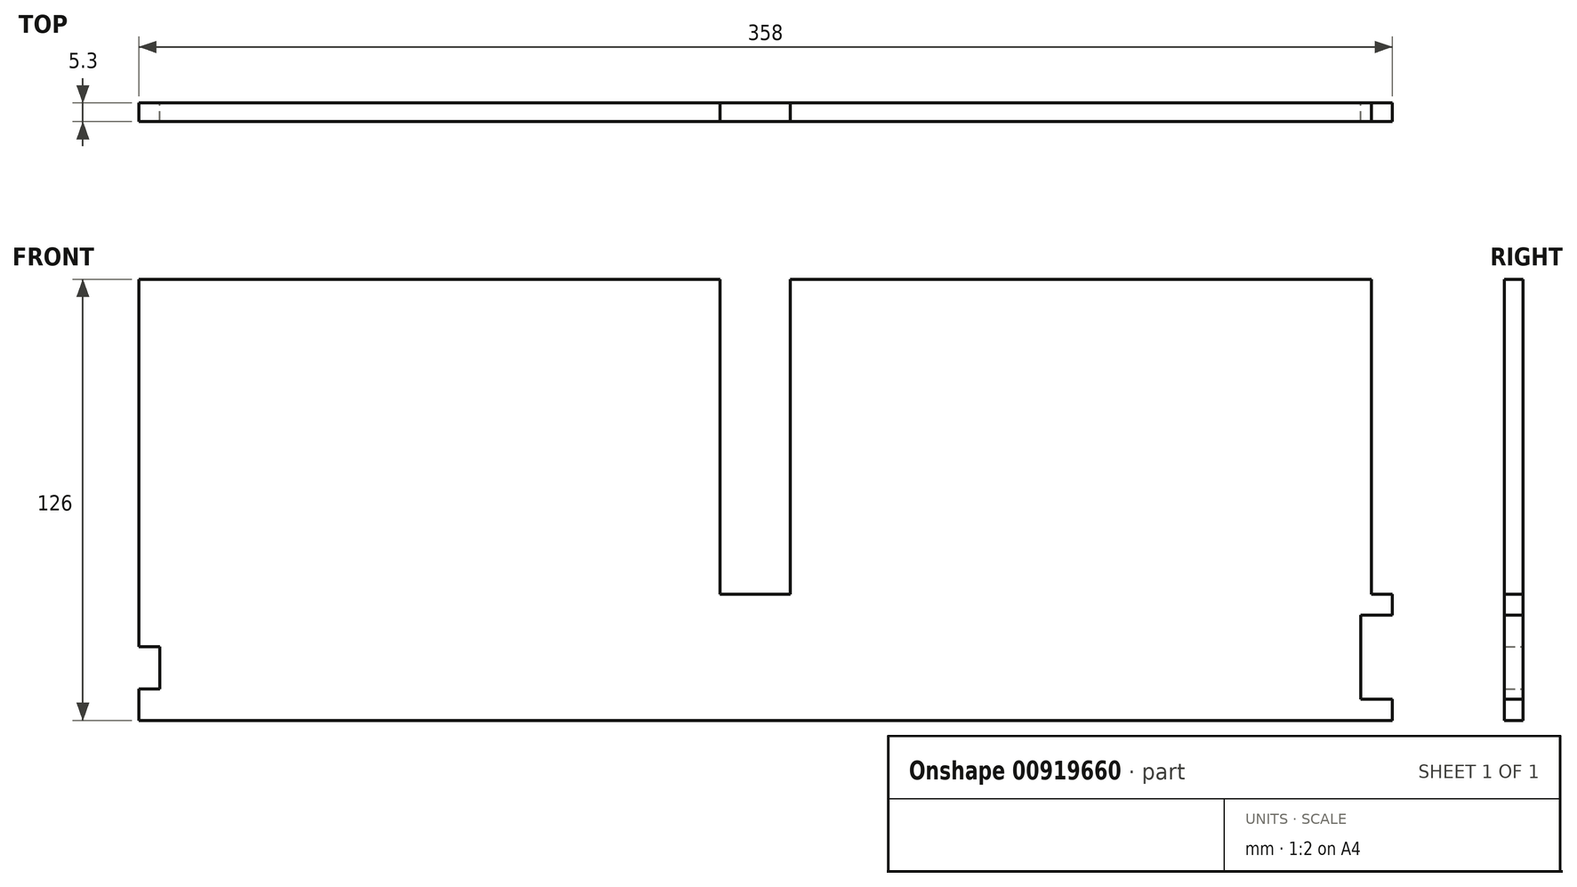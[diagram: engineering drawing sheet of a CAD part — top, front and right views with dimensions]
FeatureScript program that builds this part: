
annotation { "Feature Type Name" : "Feature", "Feature Type Description" : "" }
export const myFeature = defineFeature(function(context is Context, id is Id, definition is map)
    precondition{}
    {
        {
            var Q0;
            Q0=qCreatedBy(makeId("Front.planeOp"),FACE);
            var sketch = newSketch(context, id + "F0", { "sketchPlane" : qUnion([Q0])});
            skLineSegment(sketch, "E0", {"start": v(-176, 108) * mm, "end": v(-176, 3) * mm});
            skLineSegment(sketch, "E1.MirrorCS", {"start": v(176, 108) * mm, "end": v(176, 18) * mm});
            skLineSegment(sketch, "E2", {"start": v(176, 18) * mm, "end": v(182, 18) * mm});
            skLineSegment(sketch, "E3", {"start": v(182, 18) * mm, "end": v(182, 12) * mm});
            skLineSegment(sketch, "E4", {"start": v(182, 12) * mm, "end": v(173, 12) * mm});
            skLineSegment(sketch, "E5", {"start": v(173, 12) * mm, "end": v(173, -12) * mm});
            skLineSegment(sketch, "E6", {"start": v(173, -12) * mm, "end": v(182, -12) * mm});
            skLineSegment(sketch, "E7", {"start": v(182, -12) * mm, "end": v(182, -18) * mm});
            skLineSegment(sketch, "E8", {"start": v(-176, -18) * mm, "end": v(182, -18) * mm});
            skLineSegment(sketch, "E9", {"start": v(-170, 3) * mm, "end": v(-170, -9) * mm});
            skLineSegment(sketch, "E10", {"start": v(-176, -18) * mm, "end": v(-176, -18) * mm});
            skLineSegment(sketch, "E11", {"start": v(-176, -18) * mm, "end": v(-176, -9) * mm});
            skLineSegment(sketch, "E12", {"start": v(-176, -9) * mm, "end": v(-170, -9) * mm});
            skLineSegment(sketch, "E13", {"start": v(-170, 3) * mm, "end": v(-176, 3) * mm});
            skPoint(sketch, "E14", {"position": v(-170, -3) * mm});
            skLineSegment(sketch, "E15", {"start": v(-10, 108) * mm, "end": v(-10, 18) * mm});
            skLineSegment(sketch, "E16", {"start": v(-10, 18) * mm, "end": v(10, 18) * mm});
            skLineSegment(sketch, "E17", {"start": v(10, 18) * mm, "end": v(10, 108) * mm});
            skLineSegment(sketch, "E18", {"start": v(-176, 108) * mm, "end": v(-10, 108) * mm});
            skLineSegment(sketch, "E19", {"start": v(10, 108) * mm, "end": v(176, 108) * mm});
            skSolve(sketch);
        }
        {
            var Q0;
            Q0=qSketchRegion(id+"F0",true);
            extrude(context, id + "F1", {"entities" : qUnion([Q0]), "depth" : 5.3 * mm, "offsetDistance" : 25 * mm});
        }
    });
